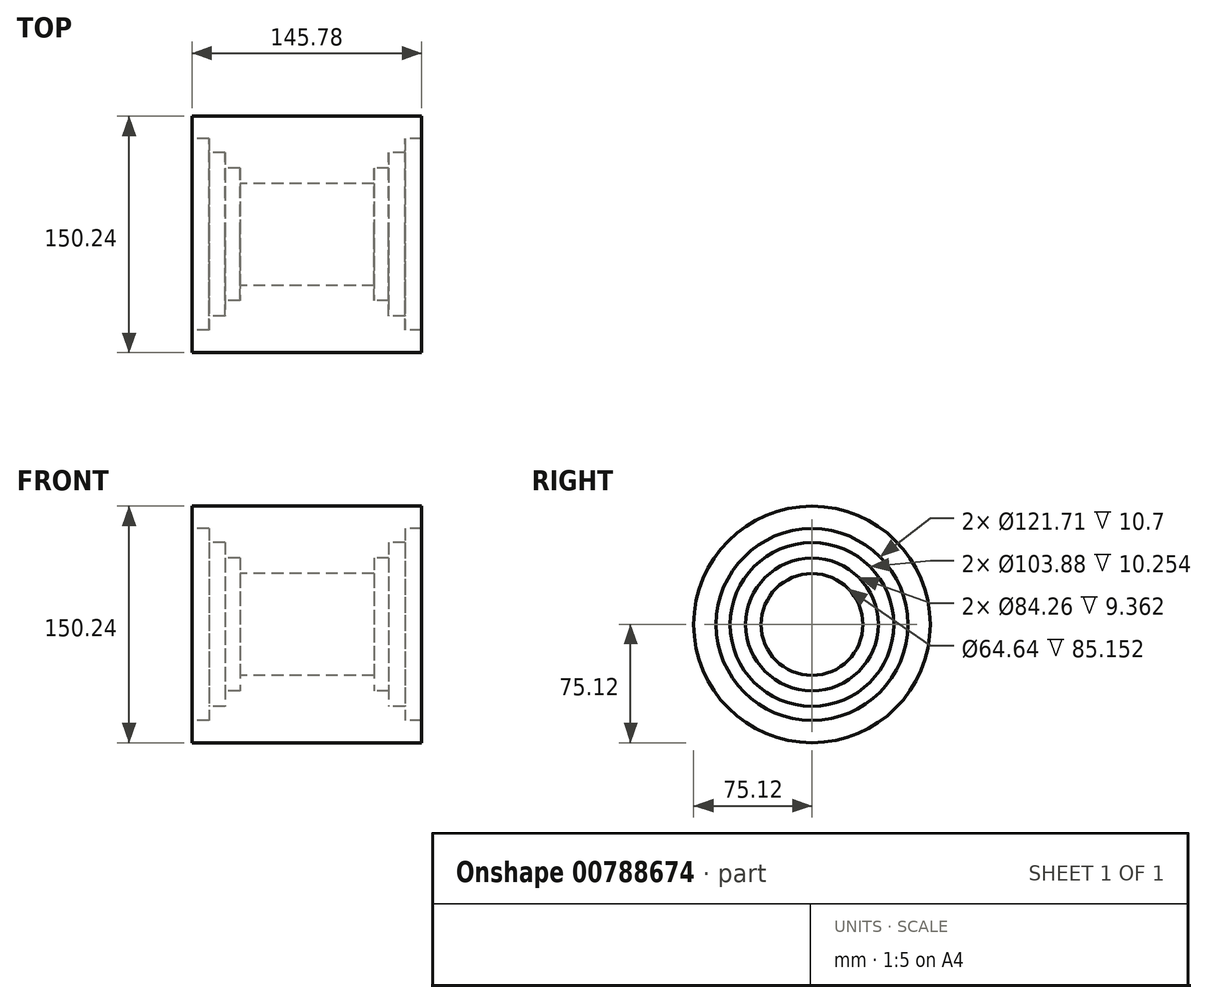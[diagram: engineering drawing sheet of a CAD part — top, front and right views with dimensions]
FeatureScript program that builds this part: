
annotation { "Feature Type Name" : "Feature", "Feature Type Description" : "" }
export const myFeature = defineFeature(function(context is Context, id is Id, definition is map)
    precondition{}
    {
        {
            var Q0;
            Q0=qCreatedBy(makeId("Front.planeOp"),FACE);
            var sketch = newSketch(context, id + "F0", { "sketchPlane" : qUnion([Q0])});
            skLineSegment(sketch, "E0", {"start": v(0, 0) * mm, "end": v(0, 75.12) * mm});
            skLineSegment(sketch, "E1", {"start": v(0, 75.12) * mm, "end": v(72.9, 75.12) * mm});
            skLineSegment(sketch, "E2", {"start": v(72.9, 75.12) * mm, "end": v(72.9, 60.85) * mm});
            skLineSegment(sketch, "E3", {"start": v(72.9, 60.85) * mm, "end": v(62.2, 60.85) * mm});
            skLineSegment(sketch, "E4", {"start": v(62.2, 60.85) * mm, "end": v(62.2, 51.94) * mm});
            skLineSegment(sketch, "E5", {"start": v(62.2, 51.94) * mm, "end": v(51.94, 51.94) * mm});
            skLineSegment(sketch, "E6", {"start": v(51.94, 51.94) * mm, "end": v(51.94, 42.13) * mm});
            skLineSegment(sketch, "E7", {"start": v(51.94, 42.13) * mm, "end": v(42.58, 42.13) * mm});
            skLineSegment(sketch, "E8", {"start": v(42.58, 42.13) * mm, "end": v(42.58, 32.32) * mm});
            skLineSegment(sketch, "E9", {"start": v(42.58, 32.32) * mm, "end": v(0, 32.32) * mm});
            skLineSegment(sketch, "E10.MirrorCS", {"start": v(0, 75.12) * mm, "end": v(-72.9, 75.12) * mm});
            skLineSegment(sketch, "E11.MirrorCS", {"start": v(-72.9, 75.12) * mm, "end": v(-72.9, 60.85) * mm});
            skLineSegment(sketch, "E12.MirrorCS", {"start": v(-72.9, 60.85) * mm, "end": v(-62.2, 60.85) * mm});
            skLineSegment(sketch, "E13.MirrorCS", {"start": v(-62.2, 60.85) * mm, "end": v(-62.2, 51.94) * mm});
            skLineSegment(sketch, "E14.MirrorCS", {"start": v(-62.2, 51.94) * mm, "end": v(-51.94, 51.94) * mm});
            skLineSegment(sketch, "E15.MirrorCS", {"start": v(-51.94, 51.94) * mm, "end": v(-51.94, 42.13) * mm});
            skLineSegment(sketch, "E16.MirrorCS", {"start": v(-51.94, 42.13) * mm, "end": v(-42.58, 42.13) * mm});
            skLineSegment(sketch, "E17.MirrorCS", {"start": v(-42.58, 42.13) * mm, "end": v(-42.58, 32.32) * mm});
            skLineSegment(sketch, "E18.MirrorCS", {"start": v(-42.58, 32.32) * mm, "end": v(0, 32.32) * mm});
            skLineSegment(sketch, "E19", {"start": v(-41.24, 0) * mm, "end": v(43.02, 0) * mm});
            skSolve(sketch);
        }
        {
            var Q0;
            Q0 = qSketchRegion(id + "F0", true);
            var Q1;
            Q1=sQuery(id+"F0.wireOp",EDGE,"E19");
            revolve(context, id + "F1", {"surfaceOperationType" : NewSurfaceOperationType.NEW, "entities" : qUnion([Q0]), "axis" : qUnion([Q1]), "revolveType" : RevolveType.FULL});
        }
    });
